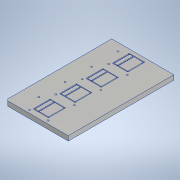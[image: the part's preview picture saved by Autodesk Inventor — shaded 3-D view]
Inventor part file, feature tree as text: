
AUTODESK INVENTOR PART (.ipt)
format: ipt  version: 2022 (Build 260153000, 153)  size: 361,984 bytes
history: native  units: in
note: dims shown in document units (in); Inventor stores cm internally (conversion verified against a paired STEP export)
features: extrude x3, sketch x3, chamfer x1
ambient origin geometry x8: Origin, YZ Plane, XZ Plane, XY Plane, X Axis, Y Axis, Z Axis, Center Point
bodies: Solid1 (feature_tree)
feature tree (7):
  extrude  "Extrusion1"  Depth=8.5in
  chamfer  "Chamfer1"  Distance=0.375in
  extrude  "Extrusion10"  Depth=0.125in
  extrude  "Extrusion11"  Depth=0.3937in
  sketch  "Sketch1"  dims[d0=5.0in d1=8.5in d2=0.375in d3=0.0in]
  sketch  "Sketch12"  dims[d126=0.125in d127=0.125in d128=45.0deg d166=0.125in]
  sketch  "Sketch13"  dims[d167=1.5in d169=0.5in d170=1.25in d171=1.0in d172=0.0in d173=0.0787in d174=0.3543in d175=0.3543in d176=1.75in d177=0.75in d178=0.5in d179=0.125in d187=1.5748in d189=2.2566in d190=0.3937in d192=1.0in d194=1.5748in d196=2.125in d197=0.3937in d199=1.0in d201=0.0625in d202=0.0625in d203=0.0625in d204=0.0625in d205=0.0625in d210=0.2756in d211=0.0625in d212=0.0625in d213=0.75in d221=0.0625in d222=0.0in d223=0.4579in d224=1.375in d232=0.0312in d233=1.5748in d235=2.125in d236=0.3937in d238=1.0in]
